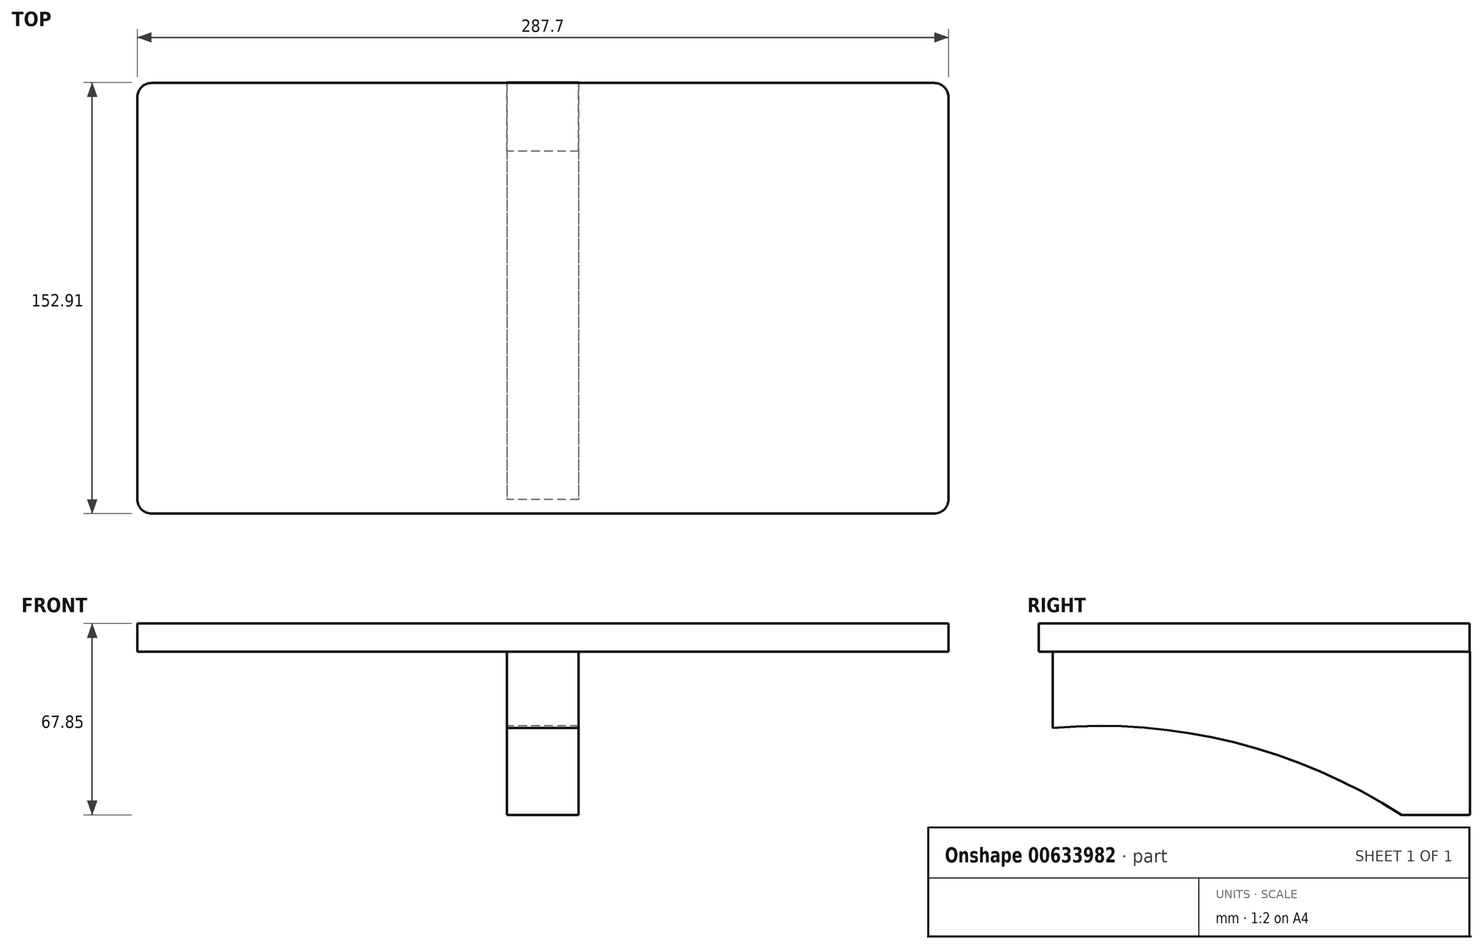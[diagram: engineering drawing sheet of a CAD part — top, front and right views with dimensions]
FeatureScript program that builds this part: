
annotation { "Feature Type Name" : "Feature", "Feature Type Description" : "" }
export const myFeature = defineFeature(function(context is Context, id is Id, definition is map)
    precondition{}
    {
        {
            var Q0;
            Q0=qCreatedBy(makeId("Top.planeOp"),FACE);
            var sketch = newSketch(context, id + "F0", { "sketchPlane" : qUnion([Q0])});
            skLineSegment(sketch, "E0.bottom", {"start": v(143.85, 76.38) * mm, "end": v(-143.85, 76.38) * mm});
            skLineSegment(sketch, "E0.top", {"start": v(143.85, -76.38) * mm, "end": v(-143.85, -76.38) * mm});
            skLineSegment(sketch, "E0.left", {"start": v(143.85, 76.38) * mm, "end": v(143.85, -76.38) * mm});
            skLineSegment(sketch, "E0.right", {"start": v(-143.85, 76.38) * mm, "end": v(-143.85, -76.38) * mm});
            skPoint(sketch, "E0.middle", {"position": v(0, 0) * mm});
            skSolve(sketch);
        }
        {
            var Q0;
            Q0 = qSketchRegion(id + "F0", true);
            extrude(context, id + "F1", {"entities" : qUnion([Q0]), "depth" : 10 * mm, "offsetDistance" : 25.4 * mm});
        }
        {
            var Q0;
            Q0=makeQuery(id+"F1.opExtrude","SWEPT_EDGE",EDGE,{"disambiguationData":[OSD([sQuery(id+"F0.wireOp",EDGE,"E0.top"),sQuery(id+"F0.wireOp",EDGE,"E0.left")])]});
            var Q1;
            Q1=makeQuery(id+"F1.opExtrude","SWEPT_EDGE",EDGE,{"disambiguationData":[OSD([sQuery(id+"F0.wireOp",EDGE,"E0.bottom"),sQuery(id+"F0.wireOp",EDGE,"E0.right")])]});
            var Q2;
            Q2=makeQuery(id+"F1.opExtrude","SWEPT_EDGE",EDGE,{"disambiguationData":[OSD([sQuery(id+"F0.wireOp",EDGE,"E0.top"),sQuery(id+"F0.wireOp",EDGE,"E0.right")])]});
            var Q3;
            Q3=makeQuery(id+"F1.opExtrude","SWEPT_EDGE",EDGE,{"disambiguationData":[OSD([sQuery(id+"F0.wireOp",EDGE,"E0.bottom"),sQuery(id+"F0.wireOp",EDGE,"E0.left")])]});
            fillet(context, id + "F2", {"entities" : qUnion([Q0, Q1, Q2, Q3]), "radius" : 5.08 * mm, "tangentPropagation" : true, "allowEdgeOverflow" : false});
        }
        {
            var Q0;
            Q0=qCreatedBy(makeId("Right.planeOp"),FACE);
            var sketch = newSketch(context, id + "F3", { "sketchPlane" : qUnion([Q0])});
            skLineSegment(sketch, "E1", {"start": v(0, 0) * mm, "end": v(-71.38, 0) * mm});
            skLineSegment(sketch, "E2", {"start": v(-71.38, 0) * mm, "end": v(-71.38, -27) * mm});
            skArc(sketch, "E3", {"start": v(52.2, -57.85) * mm, "mid": v(-7.03, -32.18) * mm, "end": v(-71.38, -27) * mm});
            skLineSegment(sketch, "E4", {"start": v(52.2, -57.85) * mm, "end": v(76.53, -57.85) * mm});
            skLineSegment(sketch, "E5", {"start": v(76.53, -57.85) * mm, "end": v(76.53, 0) * mm});
            skLineSegment(sketch, "E6", {"start": v(76.53, 0) * mm, "end": v(0, 0) * mm});
            skSolve(sketch);
        }
        {
            var Q0;
            Q0 = qSketchRegion(id + "F3", true);
            extrude(context, id + "F4", {"entities" : qUnion([Q0]), "operationType" : NewBodyOperationType.ADD, "endBound" : BoundingType.SYMMETRIC, "depth" : 25.4 * mm, "offsetDistance" : 25.4 * mm});
        }
    });
